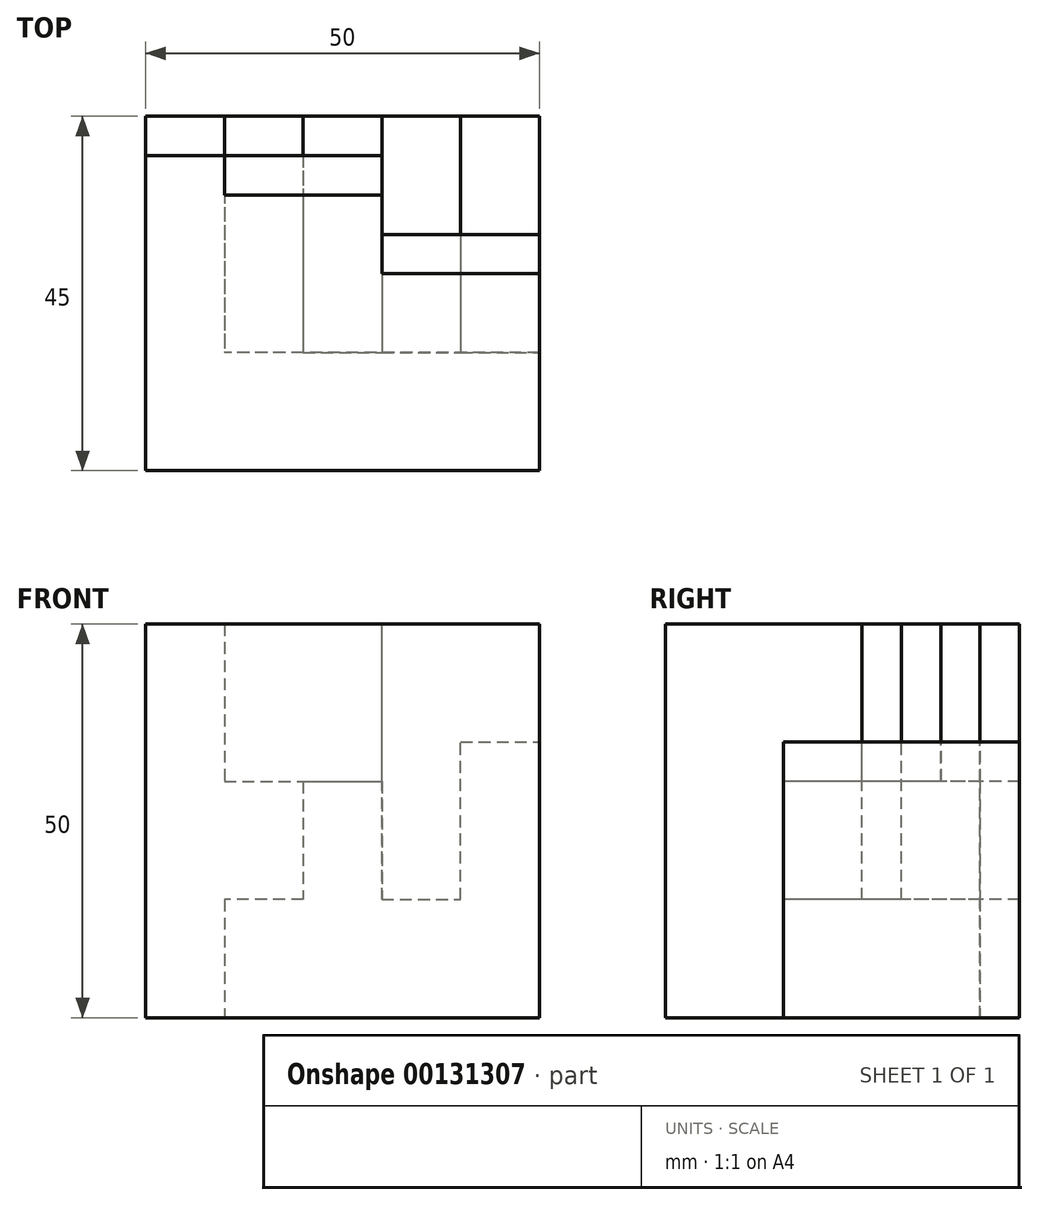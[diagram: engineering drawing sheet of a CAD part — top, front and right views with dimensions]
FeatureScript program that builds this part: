
annotation { "Feature Type Name" : "Feature", "Feature Type Description" : "" }
export const myFeature = defineFeature(function(context is Context, id is Id, definition is map)
    precondition{}
    {
        {
            var Q0;
            Q0=qCreatedBy(makeId("Front.planeOp"),FACE);
            var sketch = newSketch(context, id + "F0", { "sketchPlane" : qUnion([Q0])});
            skLineSegment(sketch, "E0.bottom", {"start": v(25, -25) * mm, "end": v(-25, -25) * mm});
            skLineSegment(sketch, "E0.top", {"start": v(25, 25) * mm, "end": v(-25, 25) * mm});
            skLineSegment(sketch, "E0.left", {"start": v(25, -25) * mm, "end": v(25, 25) * mm});
            skLineSegment(sketch, "E0.right", {"start": v(-25, -25) * mm, "end": v(-25, 25) * mm});
            skPoint(sketch, "E0.middle", {"position": v(0, 0) * mm});
            skLineSegment(sketch, "E1", {"start": v(-15, 25) * mm, "end": v(-15, 5) * mm});
            skLineSegment(sketch, "E2", {"start": v(-15, 5) * mm, "end": v(-5, 5) * mm});
            skPoint(sketch, "E3.endSnap0", {"position": v(0, -25) * mm});
            skLineSegment(sketch, "E4", {"start": v(-5, 5) * mm, "end": v(5, 5) * mm});
            skLineSegment(sketch, "E5", {"start": v(5, 5) * mm, "end": v(5, 25) * mm});
            skLineSegment(sketch, "E6", {"start": v(5, 5) * mm, "end": v(5, -10) * mm});
            skLineSegment(sketch, "E7", {"start": v(5, -10) * mm, "end": v(15, -10) * mm});
            skLineSegment(sketch, "E8", {"start": v(15, -10) * mm, "end": v(15, 10) * mm});
            skLineSegment(sketch, "E9", {"start": v(15, 10) * mm, "end": v(25, 10) * mm});
            skLineSegment(sketch, "E10", {"start": v(-5, 5) * mm, "end": v(-5, -10) * mm});
            skLineSegment(sketch, "E11", {"start": v(-5, -10) * mm, "end": v(-15, -10) * mm});
            skLineSegment(sketch, "E12", {"start": v(-15, -10) * mm, "end": v(-15, -25) * mm});
            skSolve(sketch);
        }
        {
            var Q0;
            Q0=makeQuery(id+"F0.imprint","IMPRINT",FACE,{"disambiguationData":[TD([[makeQuery(id+"F0.imprint","IMPRINT",EDGE,{"derivedFrom":sQuery(id+"F0.wireOp",EDGE,"E4")}),-1.0]])]});
            extrude(context, id + "F1", {"entities" : qUnion([Q0]), "oppositeDirection" : true, "depth" : 15 * mm});
        }
        {
            var Q0;
            {var subQ0=sQuery(id+"F0.wireOp",EDGE,"E5");Q0=makeQuery(id+"F0.imprint","IMPRINT",FACE,{"disambiguationData":[TD([[makeQuery(id+"F0.imprint","IMPRINT",EDGE,{"derivedFrom":subQ0}),-1.0]])]});}
            extrude(context, id + "F2", {"entities" : qUnion([Q0]), "oppositeDirection" : true, "depth" : 25 * mm});
        }
        {
            var Q0;
            {var subQ0=sQuery(id+"F0.wireOp",EDGE,"E1");Q0=makeQuery(id+"F0.imprint","IMPRINT",FACE,{"disambiguationData":[TD([[makeQuery(id+"F0.imprint","IMPRINT",EDGE,{"derivedFrom":subQ0}),1.0]])]});}
            extrude(context, id + "F3", {"entities" : qUnion([Q0]), "oppositeDirection" : true, "depth" : 5 * mm});
        }
        {
            var Q0;
            {var subQ1=sQuery(id+"F0.wireOp",EDGE,"E0.right");Q0=makeQuery(id+"F0.imprint","IMPRINT",FACE,{"disambiguationData":[TD([[makeQuery(id+"F0.imprint","IMPRINT",EDGE,{"derivedFrom":subQ1}),-1.0]])]});}
            extrude(context, id + "F4", {"entities" : qUnion([Q0]), "operationType" : NewBodyOperationType.ADD, "oppositeDirection" : true, "depth" : 10 * mm});
        }
        {
            var Q0;
            Q0=makeQuery(id+"F3.opExtrude","CAP_FACE",FACE,{"disambiguationData":[OSD([sQuery(id+"F0.wireOp",EDGE,"E0.top"),sQuery(id+"F0.wireOp",EDGE,"E1"),sQuery(id+"F0.wireOp",EDGE,"E2"),sQuery(id+"F0.wireOp",EDGE,"E4"),sQuery(id+"F0.wireOp",EDGE,"E5")])],"isStart":false});
            var Q1;
            Q1=makeQuery(id+"F4.opExtrude","CAP_FACE",FACE,{"disambiguationData":[OSD([sQuery(id+"F0.wireOp",EDGE,"E0.bottom"),sQuery(id+"F0.wireOp",EDGE,"E0.top"),sQuery(id+"F0.wireOp",EDGE,"E0.right"),sQuery(id+"F0.wireOp",EDGE,"E1"),sQuery(id+"F0.wireOp",EDGE,"E2"),sQuery(id+"F0.wireOp",EDGE,"E10"),sQuery(id+"F0.wireOp",EDGE,"E11"),sQuery(id+"F0.wireOp",EDGE,"E12")])],"isStart":false});
            extrude(context, id + "F5", {"entities" : qUnion([Q0, Q1]), "depth" : 10 * mm});
        }
        {
            var Q0;
            Q0=makeQuery(id+"F1.opExtrude","CAP_FACE",FACE,{"disambiguationData":[OSD([sQuery(id+"F0.wireOp",EDGE,"E0.bottom"),sQuery(id+"F0.wireOp",EDGE,"E0.left"),sQuery(id+"F0.wireOp",EDGE,"E4"),sQuery(id+"F0.wireOp",EDGE,"E6"),sQuery(id+"F0.wireOp",EDGE,"E7"),sQuery(id+"F0.wireOp",EDGE,"E8"),sQuery(id+"F0.wireOp",EDGE,"E9"),sQuery(id+"F0.wireOp",EDGE,"E10"),sQuery(id+"F0.wireOp",EDGE,"E11"),sQuery(id+"F0.wireOp",EDGE,"E12")])],"isStart":false});
            var Q1;
            Q1=makeQuery(id+"F2.opExtrude","CAP_FACE",FACE,{"disambiguationData":[OSD([sQuery(id+"F0.wireOp",EDGE,"E0.top"),sQuery(id+"F0.wireOp",EDGE,"E0.left"),sQuery(id+"F0.wireOp",EDGE,"E5"),sQuery(id+"F0.wireOp",EDGE,"E6"),sQuery(id+"F0.wireOp",EDGE,"E7"),sQuery(id+"F0.wireOp",EDGE,"E8"),sQuery(id+"F0.wireOp",EDGE,"E9")])],"isStart":false});
            extrude(context, id + "F6", {"entities" : qUnion([Q0, Q1]), "oppositeDirection" : true, "depth" : 15 * mm});
        }
        {
            var Q0;
            Q0=makeQuery(id+"F5.opExtrude","CAP_FACE",FACE,{"disambiguationData":[OSD([sQuery(id+"F0.wireOp",EDGE,"E0.top"),sQuery(id+"F0.wireOp",EDGE,"E1"),sQuery(id+"F0.wireOp",EDGE,"E2"),sQuery(id+"F0.wireOp",EDGE,"E4"),sQuery(id+"F0.wireOp",EDGE,"E5")])],"isStart":false});
            var Q1;
            Q1=makeQuery(id+"F5.opExtrude","CAP_FACE",FACE,{"disambiguationData":[OSD([sQuery(id+"F0.wireOp",EDGE,"E0.bottom"),sQuery(id+"F0.wireOp",EDGE,"E0.top"),sQuery(id+"F0.wireOp",EDGE,"E0.right"),sQuery(id+"F0.wireOp",EDGE,"E1"),sQuery(id+"F0.wireOp",EDGE,"E2"),sQuery(id+"F0.wireOp",EDGE,"E10"),sQuery(id+"F0.wireOp",EDGE,"E11"),sQuery(id+"F0.wireOp",EDGE,"E12")])],"isStart":false});
            extrude(context, id + "F7", {"entities" : qUnion([Q0, Q1]), "operationType" : NewBodyOperationType.ADD, "depth" : 20 * mm});
        }
        {
            var Q0;
            Q0=makeQuery(id+"F1.opExtrude","CAP_FACE",FACE,{"disambiguationData":[OSD([sQuery(id+"F0.wireOp",EDGE,"E0.bottom"),sQuery(id+"F0.wireOp",EDGE,"E0.left"),sQuery(id+"F0.wireOp",EDGE,"E4"),sQuery(id+"F0.wireOp",EDGE,"E6"),sQuery(id+"F0.wireOp",EDGE,"E7"),sQuery(id+"F0.wireOp",EDGE,"E8"),sQuery(id+"F0.wireOp",EDGE,"E9"),sQuery(id+"F0.wireOp",EDGE,"E10"),sQuery(id+"F0.wireOp",EDGE,"E11"),sQuery(id+"F0.wireOp",EDGE,"E12")])],"isStart":false});
            extrude(context, id + "F8", {"entities" : qUnion([Q0]), "depth" : 30 * mm});
        }
        {
            var Q0;
            Q0=makeQuery(id+"F2.opExtrude","CAP_FACE",FACE,{"disambiguationData":[OSD([sQuery(id+"F0.wireOp",EDGE,"E0.top"),sQuery(id+"F0.wireOp",EDGE,"E0.left"),sQuery(id+"F0.wireOp",EDGE,"E5"),sQuery(id+"F0.wireOp",EDGE,"E6"),sQuery(id+"F0.wireOp",EDGE,"E7"),sQuery(id+"F0.wireOp",EDGE,"E8"),sQuery(id+"F0.wireOp",EDGE,"E9")])],"isStart":false});
            var Q1;
            Q1=makeQuery(id+"F7.opExtrude","CAP_FACE",FACE,{"disambiguationData":[OSD([sQuery(id+"F0.wireOp",EDGE,"E0.top"),sQuery(id+"F0.wireOp",EDGE,"E1"),sQuery(id+"F0.wireOp",EDGE,"E2"),sQuery(id+"F0.wireOp",EDGE,"E4"),sQuery(id+"F0.wireOp",EDGE,"E5")])],"isStart":false});
            var Q2;
            Q2=makeQuery(id+"F7.opExtrude","CAP_FACE",FACE,{"disambiguationData":[OSD([sQuery(id+"F0.wireOp",EDGE,"E0.bottom"),sQuery(id+"F0.wireOp",EDGE,"E0.top"),sQuery(id+"F0.wireOp",EDGE,"E0.right"),sQuery(id+"F0.wireOp",EDGE,"E1"),sQuery(id+"F0.wireOp",EDGE,"E2"),sQuery(id+"F0.wireOp",EDGE,"E10"),sQuery(id+"F0.wireOp",EDGE,"E11"),sQuery(id+"F0.wireOp",EDGE,"E12")])],"isStart":false});
            extrude(context, id + "F9", {"entities" : qUnion([Q0, Q1, Q2]), "depth" : 5 * mm});
        }
    });
